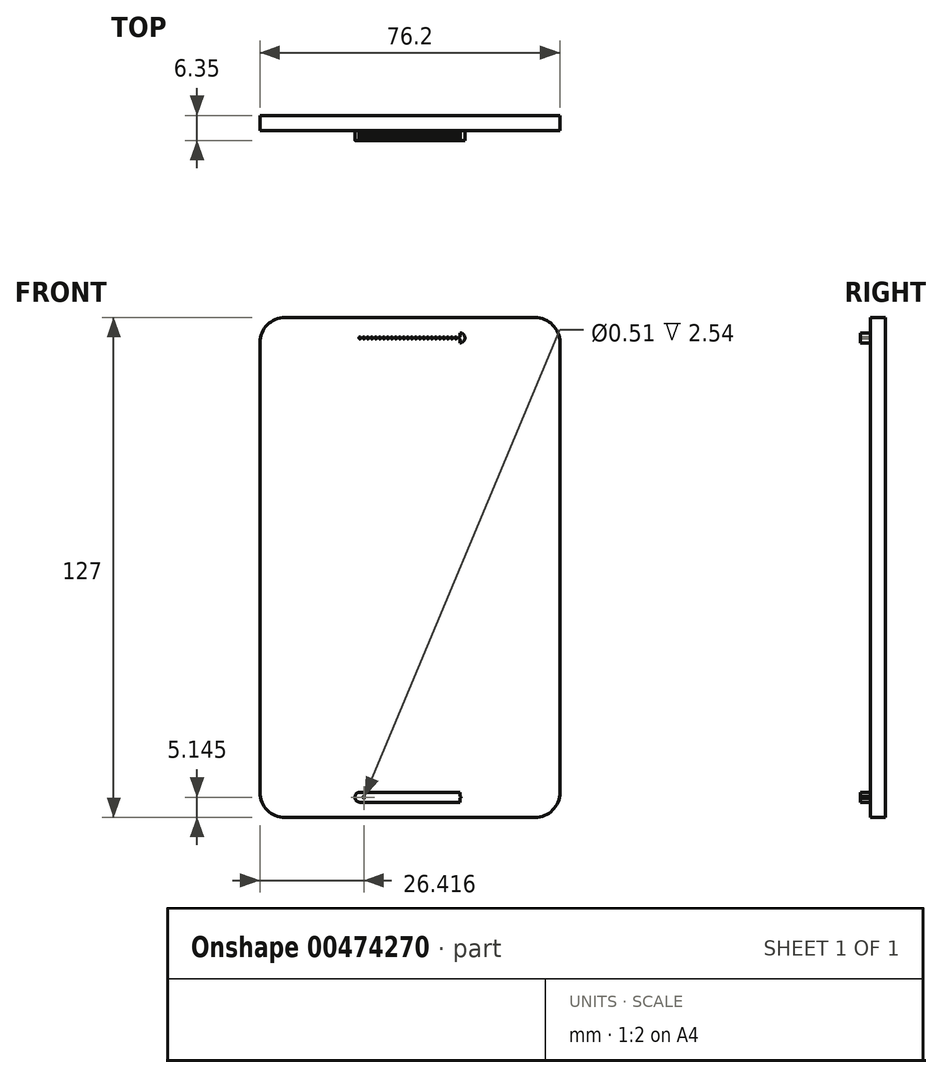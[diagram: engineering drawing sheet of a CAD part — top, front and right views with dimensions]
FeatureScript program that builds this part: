
annotation { "Feature Type Name" : "Feature", "Feature Type Description" : "" }
export const myFeature = defineFeature(function(context is Context, id is Id, definition is map)
    precondition{}
    {
        {
            var Q0;
            Q0=qCreatedBy(makeId("Front.planeOp"),FACE);
            var sketch = newSketch(context, id + "F0", { "sketchPlane" : qUnion([Q0])});
            skLineSegment(sketch, "E0", {"start": v(0, 63.5) * mm, "end": v(31.75, 63.5) * mm});
            skLineSegment(sketch, "E1", {"start": v(38.1, 57.15) * mm, "end": v(38.1, 0) * mm});
            skLineSegment(sketch, "E2", {"start": v(0, 0) * mm, "end": v(0, 63.5) * mm, "construction": true});
            skLineSegment(sketch, "E3", {"start": v(0, 0) * mm, "end": v(38.1, 0) * mm, "construction": true});
            skPoint(sketch, "E4.visualSharp", {"position": v(38.1, 63.5) * mm});
            skArc(sketch, "E4.filletArc", {"start": v(38.1, 57.15) * mm, "mid": v(36.24, 61.64) * mm, "end": v(31.75, 63.5) * mm});
            skLineSegment(sketch, "E5.MirrorCS", {"start": v(0, -63.5) * mm, "end": v(31.75, -63.5) * mm});
            skArc(sketch, "E6.MirrorCS", {"start": v(38.1, -57.15) * mm, "mid": v(36.24, -61.64) * mm, "end": v(31.75, -63.5) * mm});
            skLineSegment(sketch, "E7.MirrorCS", {"start": v(38.1, -57.15) * mm, "end": v(38.1, 0) * mm});
            skLineSegment(sketch, "E8.MirrorCS", {"start": v(0, 63.5) * mm, "end": v(-31.75, 63.5) * mm});
            skArc(sketch, "E9.MirrorCS", {"start": v(-38.1, 57.15) * mm, "mid": v(-36.24, 61.64) * mm, "end": v(-31.75, 63.5) * mm});
            skLineSegment(sketch, "E10.MirrorCS", {"start": v(-38.1, 57.15) * mm, "end": v(-38.1, 0) * mm});
            skLineSegment(sketch, "E11.MirrorCS", {"start": v(-38.1, -57.15) * mm, "end": v(-38.1, 0) * mm});
            skArc(sketch, "E12.MirrorCS", {"start": v(-38.1, -57.15) * mm, "mid": v(-36.24, -61.64) * mm, "end": v(-31.75, -63.5) * mm});
            skLineSegment(sketch, "E13.MirrorCS", {"start": v(0, -63.5) * mm, "end": v(-31.75, -63.5) * mm});
            skSolve(sketch);
        }
        {
            var Q0;
            Q0=makeQuery(id+"F0.imprint","IMPRINT",FACE,{"disambiguationData":[TD([[makeQuery(id+"F0.imprint","IMPRINT",EDGE,{"derivedFrom":sQuery(id+"F0.wireOp",EDGE,"E0")}),-1.0]])]});
            extrude(context, id + "F1", {"entities" : qUnion([Q0]), "depth" : 6.35 * mm});
        }
        {
            var Q0;
            Q0=makeQuery(id+"F1.opExtrude","CAP_FACE",FACE,{"disambiguationData":[OSD([sQuery(id+"F0.wireOp",EDGE,"E0"),sQuery(id+"F0.wireOp",EDGE,"E1"),sQuery(id+"F0.wireOp",EDGE,"E4.filletArc"),sQuery(id+"F0.wireOp",EDGE,"E5.MirrorCS"),sQuery(id+"F0.wireOp",EDGE,"E6.MirrorCS"),sQuery(id+"F0.wireOp",EDGE,"E7.MirrorCS"),sQuery(id+"F0.wireOp",EDGE,"E8.MirrorCS"),sQuery(id+"F0.wireOp",EDGE,"E9.MirrorCS"),sQuery(id+"F0.wireOp",EDGE,"E10.MirrorCS"),sQuery(id+"F0.wireOp",EDGE,"E11.MirrorCS"),sQuery(id+"F0.wireOp",EDGE,"E12.MirrorCS"),sQuery(id+"F0.wireOp",EDGE,"E13.MirrorCS")])],"isStart":false});
            var sketch = newSketch(context, id + "F2", { "sketchPlane" : qUnion([Q0])});
            skLineSegment(sketch, "E14", {"start": v(0, 63.5) * mm, "end": v(0, -63.5) * mm, "construction": true});
            skLineSegment(sketch, "E15", {"start": v(-38.1, 0) * mm, "end": v(38.1, 0) * mm, "construction": true});
            skLineSegment(sketch, "E16.bottom", {"start": v(12.7, 57.08) * mm, "end": v(-12.7, 57.08) * mm});
            skLineSegment(sketch, "E16.top", {"start": v(12.7, 59.62) * mm, "end": v(-12.7, 59.62) * mm});
            skLineSegment(sketch, "E16.left", {"start": v(12.7, 57.08) * mm, "end": v(12.7, 59.62) * mm});
            skLineSegment(sketch, "E16.right", {"start": v(-12.7, 57.08) * mm, "end": v(-12.7, 59.62) * mm});
            skPoint(sketch, "E16.middle", {"position": v(0, 58.35) * mm});
            skArc(sketch, "E17", {"start": v(-12.7, 59.62) * mm, "mid": v(-13.97, 58.35) * mm, "end": v(-12.7, 57.08) * mm});
            skArc(sketch, "E18", {"start": v(12.7, 59.62) * mm, "mid": v(13.97, 58.35) * mm, "end": v(12.7, 57.08) * mm});
            skCircle(sketch, "E19", {"center": v(-12.7, 58.35) * mm, "radius": 0.25 * mm});
            skCircle(sketch, "E20.1.0.0", {"center": v(-11.68, 58.35) * mm, "radius": 0.25 * mm});
            skCircle(sketch, "E20.2.0.0", {"center": v(-10.67, 58.35) * mm, "radius": 0.25 * mm});
            skCircle(sketch, "E20.3.0.0", {"center": v(-9.65, 58.35) * mm, "radius": 0.25 * mm});
            skCircle(sketch, "E20.4.0.0", {"center": v(-8.64, 58.35) * mm, "radius": 0.25 * mm});
            skCircle(sketch, "E20.5.0.0", {"center": v(-7.62, 58.35) * mm, "radius": 0.25 * mm});
            skCircle(sketch, "E20.6.0.0", {"center": v(-6.6, 58.35) * mm, "radius": 0.25 * mm});
            skCircle(sketch, "E20.7.0.0", {"center": v(-5.59, 58.35) * mm, "radius": 0.25 * mm});
            skCircle(sketch, "E20.8.0.0", {"center": v(-4.57, 58.35) * mm, "radius": 0.25 * mm});
            skCircle(sketch, "E20.9.0.0", {"center": v(-3.56, 58.35) * mm, "radius": 0.25 * mm});
            skCircle(sketch, "E20.10.0.0", {"center": v(-2.54, 58.35) * mm, "radius": 0.25 * mm});
            skCircle(sketch, "E20.11.0.0", {"center": v(-1.52, 58.35) * mm, "radius": 0.25 * mm});
            skCircle(sketch, "E20.12.0.0", {"center": v(-0.5, 58.35) * mm, "radius": 0.25 * mm});
            skLineSegment(sketch, "E20.direction1", {"start": v(-12.7, 58.35) * mm, "end": v(-11.68, 58.35) * mm, "construction": true});
            skCircle(sketch, "E21.MirrorC", {"center": v(0.5, 58.35) * mm, "radius": 0.25 * mm});
            skCircle(sketch, "E22.MirrorC", {"center": v(1.52, 58.35) * mm, "radius": 0.25 * mm});
            skCircle(sketch, "E23.MirrorC", {"center": v(2.54, 58.35) * mm, "radius": 0.25 * mm});
            skCircle(sketch, "E24.MirrorC", {"center": v(3.56, 58.35) * mm, "radius": 0.25 * mm});
            skCircle(sketch, "E25.MirrorC", {"center": v(4.57, 58.35) * mm, "radius": 0.25 * mm});
            skCircle(sketch, "E26.MirrorC", {"center": v(5.59, 58.35) * mm, "radius": 0.25 * mm});
            skCircle(sketch, "E27.MirrorC", {"center": v(6.6, 58.35) * mm, "radius": 0.25 * mm});
            skCircle(sketch, "E28.MirrorC", {"center": v(7.62, 58.35) * mm, "radius": 0.25 * mm});
            skCircle(sketch, "E29.MirrorC", {"center": v(8.64, 58.35) * mm, "radius": 0.25 * mm});
            skCircle(sketch, "E30.MirrorC", {"center": v(9.65, 58.35) * mm, "radius": 0.25 * mm});
            skCircle(sketch, "E31.MirrorC", {"center": v(10.67, 58.35) * mm, "radius": 0.25 * mm});
            skCircle(sketch, "E32.MirrorC", {"center": v(11.68, 58.35) * mm, "radius": 0.25 * mm});
            skCircle(sketch, "E33.MirrorC", {"center": v(12.7, 58.35) * mm, "radius": 0.25 * mm});
            skCircle(sketch, "E34.MirrorC", {"center": v(-12.7, -58.35) * mm, "radius": 0.25 * mm});
            skCircle(sketch, "E35.MirrorC", {"center": v(-0.5, -58.35) * mm, "radius": 0.25 * mm});
            skCircle(sketch, "E36.MirrorC", {"center": v(-11.68, -58.35) * mm, "radius": 0.25 * mm});
            skCircle(sketch, "E37.MirrorC", {"center": v(-5.59, -58.35) * mm, "radius": 0.25 * mm});
            skCircle(sketch, "E38.MirrorC", {"center": v(-6.6, -58.35) * mm, "radius": 0.25 * mm});
            skCircle(sketch, "E39.MirrorC", {"center": v(-1.52, -58.35) * mm, "radius": 0.25 * mm});
            skLineSegment(sketch, "E40.MirrorCS", {"start": v(-12.7, -58.35) * mm, "end": v(-11.68, -58.35) * mm, "construction": true});
            skCircle(sketch, "E41.MirrorC", {"center": v(12.7, -58.35) * mm, "radius": 0.25 * mm});
            skCircle(sketch, "E42.MirrorC", {"center": v(9.65, -58.35) * mm, "radius": 0.25 * mm});
            skCircle(sketch, "E43.MirrorC", {"center": v(6.6, -58.35) * mm, "radius": 0.25 * mm});
            skCircle(sketch, "E44.MirrorC", {"center": v(5.59, -58.35) * mm, "radius": 0.25 * mm});
            skCircle(sketch, "E45.MirrorC", {"center": v(-4.57, -58.35) * mm, "radius": 0.25 * mm});
            skCircle(sketch, "E46.MirrorC", {"center": v(2.54, -58.35) * mm, "radius": 0.25 * mm});
            skCircle(sketch, "E47.MirrorC", {"center": v(-2.54, -58.35) * mm, "radius": 0.25 * mm});
            skCircle(sketch, "E48.MirrorC", {"center": v(11.68, -58.35) * mm, "radius": 0.25 * mm});
            skCircle(sketch, "E49.MirrorC", {"center": v(7.62, -58.35) * mm, "radius": 0.25 * mm});
            skCircle(sketch, "E50.MirrorC", {"center": v(-10.67, -58.35) * mm, "radius": 0.25 * mm});
            skCircle(sketch, "E51.MirrorC", {"center": v(8.64, -58.35) * mm, "radius": 0.25 * mm});
            skCircle(sketch, "E52.MirrorC", {"center": v(10.67, -58.35) * mm, "radius": 0.25 * mm});
            skCircle(sketch, "E53.MirrorC", {"center": v(0.5, -58.35) * mm, "radius": 0.25 * mm});
            skCircle(sketch, "E54.MirrorC", {"center": v(-7.62, -58.35) * mm, "radius": 0.25 * mm});
            skCircle(sketch, "E55.MirrorC", {"center": v(4.57, -58.35) * mm, "radius": 0.25 * mm});
            skCircle(sketch, "E56.MirrorC", {"center": v(3.56, -58.35) * mm, "radius": 0.25 * mm});
            skCircle(sketch, "E57.MirrorC", {"center": v(-9.65, -58.35) * mm, "radius": 0.25 * mm});
            skCircle(sketch, "E58.MirrorC", {"center": v(-3.56, -58.35) * mm, "radius": 0.25 * mm});
            skCircle(sketch, "E59.MirrorC", {"center": v(1.52, -58.35) * mm, "radius": 0.25 * mm});
            skCircle(sketch, "E60.MirrorC", {"center": v(-8.64, -58.35) * mm, "radius": 0.25 * mm});
            skPoint(sketch, "E61.MirrorP", {"position": v(0, -58.35) * mm});
            skLineSegment(sketch, "E62.MirrorCS", {"start": v(12.7, -57.08) * mm, "end": v(-12.7, -57.08) * mm});
            skArc(sketch, "E63.MirrorCS", {"start": v(12.7, -59.62) * mm, "mid": v(13.97, -58.35) * mm, "end": v(12.7, -57.08) * mm});
            skLineSegment(sketch, "E64.MirrorCS", {"start": v(12.7, -59.62) * mm, "end": v(-12.7, -59.62) * mm});
            skLineSegment(sketch, "E65.MirrorCS", {"start": v(-12.7, -57.08) * mm, "end": v(-12.7, -59.62) * mm});
            skArc(sketch, "E66.MirrorCS", {"start": v(-12.7, -59.62) * mm, "mid": v(-13.97, -58.35) * mm, "end": v(-12.7, -57.08) * mm});
            skLineSegment(sketch, "E67.MirrorCS", {"start": v(12.7, -57.08) * mm, "end": v(12.7, -59.62) * mm});
            skSolve(sketch);
        }
        {
            var Q0;
            {var subQ9=sQuery(id+"F2.wireOp",EDGE,"E16.bottom");Q0=makeQuery(id+"F2.imprint","IMPRINT",FACE,{"disambiguationData":[TD([[makeQuery(id+"F2.imprint","IMPRINT",EDGE,{"derivedFrom":subQ9}),-1.0]])]});}
            var Q1;
            {var subQ0=sQuery(id+"F2.wireOp",EDGE,"E17");Q1=makeQuery(id+"F2.imprint","IMPRINT",FACE,{"disambiguationData":[TD([[makeQuery(id+"F2.imprint","IMPRINT",EDGE,{"derivedFrom":subQ0}),1.0]])]});}
            var Q2;
            {var subQ0=sQuery(id+"F2.wireOp",EDGE,"E18");Q2=makeQuery(id+"F2.imprint","IMPRINT",FACE,{"disambiguationData":[TD([[makeQuery(id+"F2.imprint","IMPRINT",EDGE,{"derivedFrom":subQ0}),-1.0]])]});}
            var Q3;
            Q3=makeQuery(id+"F2.imprint","IMPRINT",FACE,{"disambiguationData":[TD([[makeQuery(id+"F2.imprint","IMPRINT",EDGE,{"derivedFrom":sQuery(id+"F2.wireOp",EDGE,"E36.MirrorC")}),1.0]])]});
            var Q4;
            {var subQ4=sQuery(id+"F2.wireOp",EDGE,"E63.MirrorCS");Q4=makeQuery(id+"F2.imprint","IMPRINT",FACE,{"disambiguationData":[TD([[makeQuery(id+"F2.imprint","IMPRINT",EDGE,{"derivedFrom":subQ4}),1.0]])]});}
            var Q5;
            {var subQ4=sQuery(id+"F2.wireOp",EDGE,"E66.MirrorCS");Q5=makeQuery(id+"F2.imprint","IMPRINT",FACE,{"disambiguationData":[TD([[makeQuery(id+"F2.imprint","IMPRINT",EDGE,{"derivedFrom":subQ4}),-1.0]])]});}
            extrude(context, id + "F3", {"entities" : qUnion([Q0, Q1, Q2, Q3, Q4, Q5]), "operationType" : NewBodyOperationType.REMOVE, "oppositeDirection" : true, "depth" : 2.54 * mm});
        }
    });
